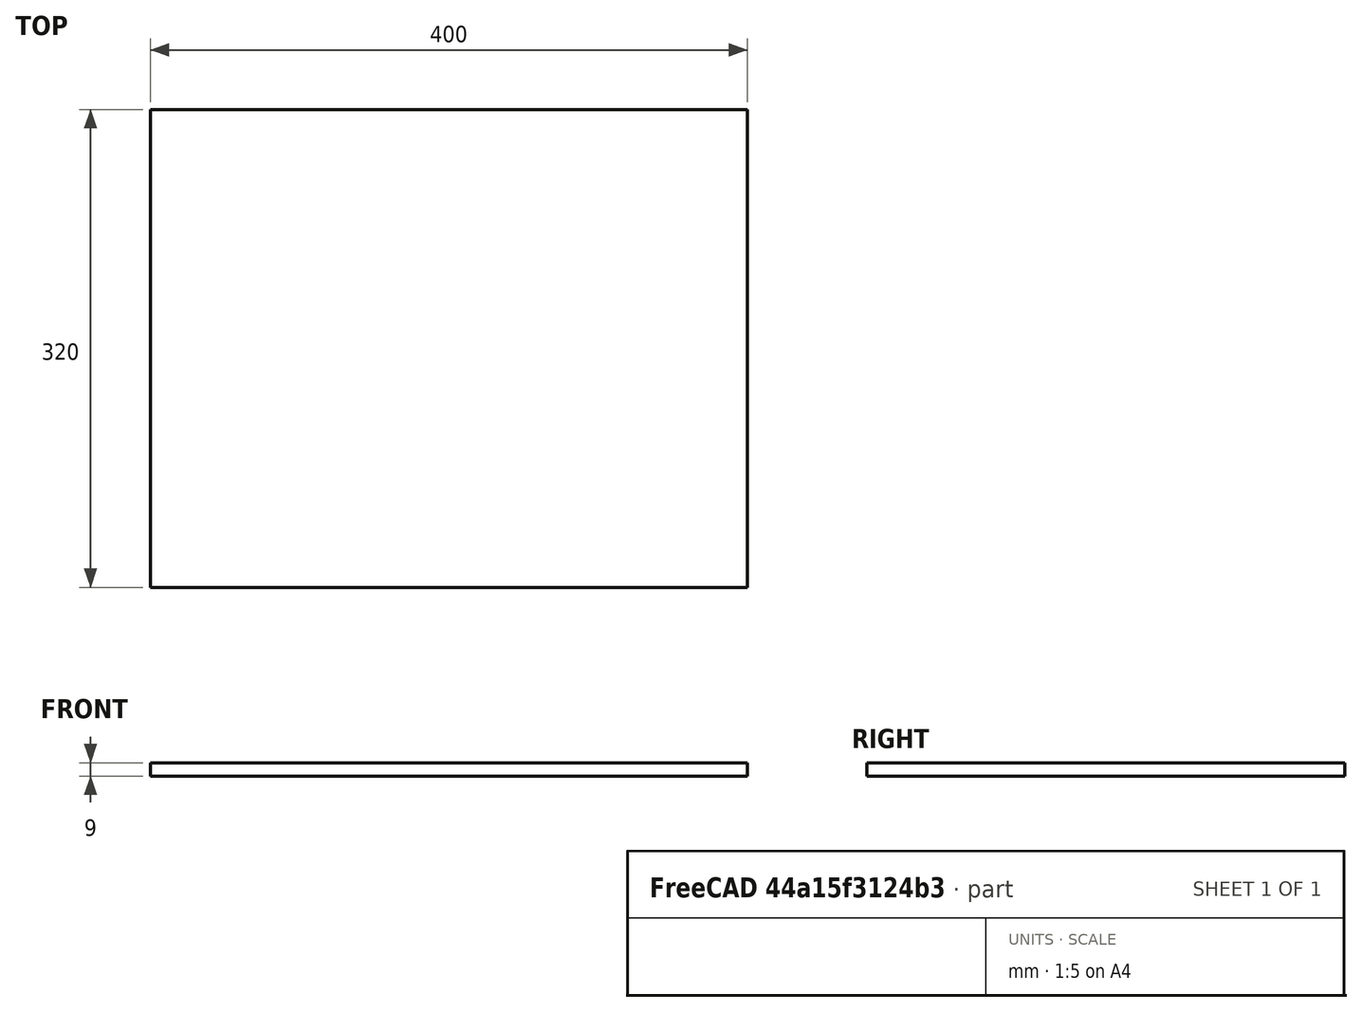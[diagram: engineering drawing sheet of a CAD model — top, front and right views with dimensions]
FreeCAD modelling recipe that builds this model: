
FCSTD DOCUMENT  (FreeCAD 0.19R)
Label: Swivel_Assembly
License: Creative Commons Attribution-ShareAlike
LicenseURL: http://creativecommons.org/licenses/by-sa/4.0/
objects: PartDesign::CoordinateSystem×2, App::DocumentObjectGroup×2, App::FeaturePython×1, Sketcher::SketchObject×1, PartDesign::Pad×1, PartDesign::Body×1, App::Link×1, App::Part×1
note: 6 computed .brp shape members not serialized (recipe doc carries the construction recipe); baked Part::Feature solids carry a one-line shape summary decoded from their .brp
EXTERNAL_REF file=../key_dimensions.FCStd obj=Spreadsheet

FEATURE [PartDesign::CoordinateSystem] LCS_Origin
  AttacherType = Attacher::AttachEngine3D
  MapMode = 2
  Support = -> [X_Axis]
FEATURE [App::DocumentObjectGroup] Constraints
FEATURE [App::FeaturePython] Variables  # WARN: FeaturePython — macro-defined, semantics opaque (R4)
FEATURE [PartDesign::CoordinateSystem] LCS_0
  AttacherType = Attacher::AttachEngine3D
  MapMode = 2
  Support = -> [X_Axis001]
FEATURE [Sketcher::SketchObject] Sketch
  FullyConstrained = true
  MapMode = 5
  Support = -> [XY_Plane001]
  expr: Constraints[10] = <<key_dimensions>>#<<Dimensions>>.base_cradle_width
  expr: Constraints[8] = <<key_dimensions>>#<<Dimensions>>.base_cradle_depth
  sketch-geometry (4):
    g0: LineSegment StartX=-200 StartY=160 StartZ=0 EndX=200 EndY=160 EndZ=0
    g1: LineSegment StartX=200 StartY=160 StartZ=0 EndX=200 EndY=-160 EndZ=0
    g2: LineSegment StartX=200 StartY=-160 StartZ=0 EndX=-200 EndY=-160 EndZ=0
    g3: LineSegment StartX=-200 StartY=-160 StartZ=0 EndX=-200 EndY=160 EndZ=0
  constraints (11):
    c: Coincident(g0,g1)
    c: Coincident(g1,g2)
    c: Coincident(g2,g3)
    c: Coincident(g3,g0)
    c: Horizontal(g0)
    c: Horizontal(g2)
    c: Vertical(g1)
    c: Vertical(g3)
    c: DistanceY(g1,g1) = 320
    c: Symmetric(g1,g0,g-1)
    c: DistanceX(g2,g2) = 400
FEATURE [PartDesign::Pad] Pad
  Direction = (1,1,1)
  Length = 9
  Length2 = 100
  Profile = -> Sketch
  Reversed = true
  Type = 0
  expr: Length = <<key_dimensions>>#<<Dimensions>>.MDF_thick
FEATURE [PartDesign::Body] Base
  Group = -> [LCS_0,Sketch,Pad]
  Origin = -> Origin001
  Tip = -> Pad
FEATURE [App::DocumentObjectGroup] Parts
  Group = -> [Base]
FEATURE [App::Link] Base001
  AssemblyType = Asm4EE
  AttachedBy = #LCS_0
  AttachedTo = Parent Assembly#LCS_Origin
  LinkedObject = -> Base
  expr: Placement = LCS_Origin.Placement * AttachmentOffset * LCS_0.Placement ^ -1
FEATURE [App::Part] Model
  Configuration = 0
  Group = -> [LCS_Origin,Constraints,Variables,Base001]
  Origin = -> Origin
  Type = Assembly4 Model

RESOLVED EXTERNAL PARTS (link-assembly join: the EXTERNAL_REF files above that resolve inside this repo's crawl, each included once):
---- part ../key_dimensions.FCStd = doc fcstd_41c4ab9f2bd9 ----
FCSTD DOCUMENT  (FreeCAD 0.19R)
Label: key_dimensions
License: Creative Commons Attribution-ShareAlike
LicenseURL: http://creativecommons.org/licenses/by-sa/4.0/
objects: Spreadsheet::Sheet×1

FEATURE [Spreadsheet::Sheet] Spreadsheet  label="Dimensions"
  cells = A1=MDF thickness; A2(MDF_thick)=9; B2=MDF thick; A3(MDF_thin)=5.5; B3=MDF thin; A4=Main Frame; A5(frame_depth)=176; B5=Frame depth; A6(frame_width)=100; B6=Frame width; A7(window_width)=690; B7=Window width; A8(center_height)=299.25; B8=Center height (base to center); A9(cradle_base)=235; B9=Cradle base (base to cradle base); A10(slider_axis_height)=190; B10=slider axis height (base to horizontal sliders axis); A11(top_height)=1150; B11=Top height (top height, without curve top); A12(rear_overhang)=400; B12=Rear overhang (from the center); A13=Acrylic; A14(acrylic_width)=330; B14=width; A15(acrylic_depth)=469; B15=depth; A16=Cradle; A17(cradle_tilting)=40; B17=cradle tilting; A18(cradle_rounded)=15; B18=cradle rounded; A19(base_cradle_width)=400; B19=Base Cradle width; A20(base_cradle_depth)=320; B20=Base Cradle depth; A21=Base Rails; A22(rail_A)=38.5; B22=Rail A; A23(rail_B)=65.5; B23=Rail B; A24(rail_C)=115.5; B24=Rail C; A25(rail_D)=140.5; B25=Rail D; A26(wing_depth)=320; B26=Wing depth; A27(wing_length)=215; B27=Wing length
